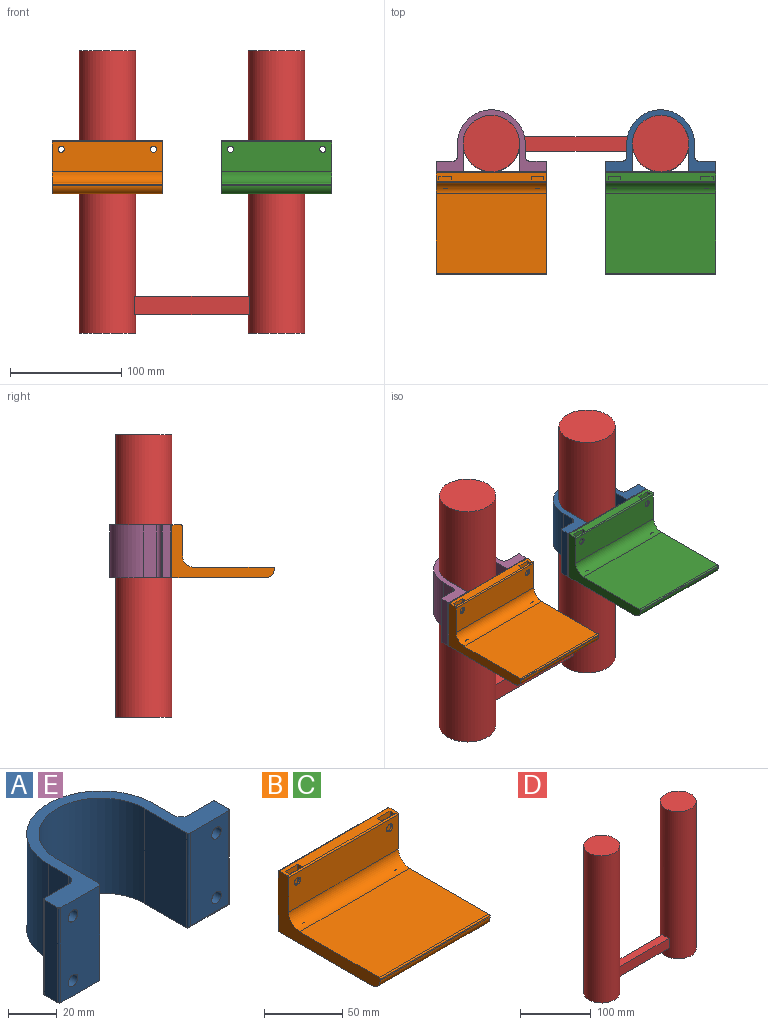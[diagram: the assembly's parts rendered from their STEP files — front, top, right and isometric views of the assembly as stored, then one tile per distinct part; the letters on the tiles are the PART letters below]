
ASSEMBLY  parts=5 mates=10
PART A: 35 faces, bbox 99.1x55.9x47.6 mm
  f0: plane 47.63x24.44mm, normal (1,0,0), area 1163.7mm2, adj f1,f12,f13,f18
  f1: cylinder r=25.4mm len=50.8mm, axis (0,0,-1), area 3800.3mm2, adj f0,f2,f12,f13
  f2: plane 47.63x24.43mm, normal (-1,0,0), area 1163.7mm2, adj f1,f12,f13,f21
  f3: plane 46.66x22.2mm, normal (0,-1,0), area 986.8mm2, adj f12,f19,f20,f21,f23,f26
  f4: plane 47.63x7.59mm, normal (1,0,0), area 361.7mm2, adj f12,f13,f19,f22
  f5: plane 47.63x14.02mm, normal (0,1,0), area 462.5mm2, adj f12,f13,f15,f22,f25,f28
  f6: plane 47.63x11.81mm, normal (1,0,0), area 562.5mm2, adj f7,f12,f13,f15
  f7: cylinder r=30.48mm len=60.96mm, axis (0,0,-1), area 4560.4mm2, adj f6,f8,f12,f13
  f8: plane 47.63x11.81mm, normal (-1,0,0), area 562.5mm2, adj f7,f12,f13,f14
  f9: plane 47.63x14.02mm, normal (0,1,0), area 462.5mm2, adj f12,f13,f14,f16,f31,f34
  f10: plane 47.63x7.59mm, normal (-1,0,0), area 361.7mm2, adj f12,f13,f16,f17
  f11: plane 47.63x22.2mm, normal (0,-1,0), area 1008.2mm2, adj f12,f13,f17,f18,f29,f32
  f12: plane 99.06x55.88mm, normal (0,0,1), area 1072.8mm2, adj f0,f1,f2,f3,f4,f5,f6,f7
  f13: plane 99.06x55.88mm, normal (0,0,-1), area 1049.9mm2, adj f0,f1,f2,f4,f5,f6,f7,f8
  f14: cylinder r=4.06mm len=47.63mm, axis (0,0,1), area 304mm2, adj f8,f9,f12,f13
  f15: cylinder r=4.06mm len=47.63mm, axis (0,0,1), area 304mm2, adj f5,f6,f12,f13
  f16: cylinder r=0.97mm len=47.63mm, axis (0,0,-1), area 72.2mm2, adj f9,f10,f12,f13
  f17: cylinder r=0.97mm len=47.63mm, axis (0,0,-1), area 72.2mm2, adj f10,f11,f12,f13
  f18: cylinder r=0.97mm len=47.63mm, axis (0,0,-1), area 72.2mm2, adj f0,f11,f12,f13
  f19: cylinder r=0.97mm len=47.63mm, axis (0,0,-1), area 71.7mm2, adj f3,f4,f12,f20
  f20: cylinder r=0.97mm len=24.13mm, axis (1,0,0), area 35.5mm2, adj f3,f13,f19,f21
  f21: cylinder r=0.97mm len=47.63mm, axis (0,0,-1), area 71.7mm2, adj f2,f3,f12,f20
  f22: cylinder r=0.97mm len=47.63mm, axis (0,0,-1), area 72.2mm2, adj f4,f5,f12,f13
  f23: cylinder r=2.79mm len=5.59mm, axis (0,1,0), area 89.2mm2, adj f3,f24
  f24: plane 11.43x11.43mm, normal (0,1,0), area 78.1mm2, adj f23,f25
  f25: cylinder r=5.71mm len=11.43mm, axis (0,1,0), area 159.6mm2, adj f5,f24
  f26: cylinder r=2.79mm len=5.59mm, axis (0,1,0), area 89.2mm2, adj f3,f27
  f27: plane 11.43x11.43mm, normal (0,1,0), area 78.1mm2, adj f26,f28
  f28: cylinder r=5.71mm len=11.43mm, axis (0,1,0), area 159.6mm2, adj f5,f27
  f29: cylinder r=2.79mm len=5.59mm, axis (0,1,0), area 89.2mm2, adj f11,f30
  f30: plane 11.43x11.43mm, normal (0,1,0), area 78.1mm2, adj f29,f31
  f31: cylinder r=5.71mm len=11.43mm, axis (0,1,0), area 159.6mm2, adj f9,f30
  f32: cylinder r=2.79mm len=5.59mm, axis (0,1,0), area 89.2mm2, adj f11,f33
  f33: plane 11.43x11.43mm, normal (0,1,0), area 78.1mm2, adj f32,f34
  f34: cylinder r=5.71mm len=11.43mm, axis (0,1,0), area 159.6mm2, adj f9,f33
PART B: 44 faces, bbox 99.1x92.1x47.6 mm
  f0: plane 99.06x7.62mm, normal (0,0,1), area 661.9mm2, adj f8,f9,f12,f15,f35,f36,f37,f38
  f1: cylinder r=2.79mm len=5.59mm, axis (0,1,0), area 22.3mm2, adj f3,f40
  f2: cylinder r=2.79mm len=5.59mm, axis (0,1,0), area 73.6mm2, adj f7,f38
  f3: plane 99.06x26.99mm, normal (0,-1,0), area 2624.3mm2, adj f1,f8,f9,f10,f12,f33
  f4: plane 99.06x71.44mm, normal (0,0,1), area 7076.6mm2, adj f8,f9,f10,f13
  f5: plane 99.06x0.95mm, normal (0,-1,0), area 94.4mm2, adj f8,f9,f11,f13
  f6: plane 99.06x83.5mm, normal (0,0,-1), area 8178.9mm2, adj f8,f9,f11,f14,f16,f17,f18,f19
  f7: plane 99.06x45.72mm, normal (0,1,0), area 4430.9mm2, adj f2,f8,f9,f14,f15,f26,f29,f32
  f8: plane 92.08x47.63mm, normal (1,0,0), area 1248.8mm2, adj f0,f3,f4,f5,f6,f7,f10,f11
  f9: plane 92.08x47.63mm, normal (-1,0,0), area 1248.8mm2, adj f0,f3,f4,f5,f6,f7,f10,f11
  f10: cylinder r=10.16mm len=99.06mm, axis (1,0,0), area 1580.9mm2, adj f3,f4,f8,f9
  f11: cylinder r=7.62mm len=99.06mm, axis (-1,0,0), area 1185.7mm2, adj f5,f6,f8,f9
  f12: cylinder r=0.95mm len=99.06mm, axis (-1,0,0), area 148.2mm2, adj f0,f3,f8,f9
  f13: cylinder r=0.95mm len=99.06mm, axis (-1,0,0), area 148.2mm2, adj f4,f5,f8,f9
  f14: cylinder r=0.95mm len=99.06mm, axis (-1,0,0), area 148.2mm2, adj f6,f7,f8,f9
  f15: cylinder r=0.95mm len=99.06mm, axis (-1,0,0), area 148.2mm2, adj f0,f7,f8,f9
  f16: plane 15.24x4.06mm, normal (1,0,0), area 61.9mm2, adj f6,f17,f19,f20
  f17: plane 15.24x11.43mm, normal (0,1,0), area 149.7mm2, adj f6,f16,f18,f20,f30
  f18: plane 15.24x4.06mm, normal (-1,0,0), area 61.9mm2, adj f6,f17,f19,f20
  f19: plane 15.24x11.43mm, normal (0,-1,0), area 149.7mm2, adj f6,f16,f18,f20,f29
  f20: plane 11.43x4.06mm, normal (0,0,-1), area 46.5mm2, adj f16,f17,f18,f19
  f21: plane 15.24x4.06mm, normal (1,0,0), area 61.9mm2, adj f6,f22,f24,f25
  f22: plane 15.24x11.43mm, normal (0,1,0), area 149.7mm2, adj f6,f21,f23,f25,f28
  f23: plane 15.24x4.06mm, normal (-1,0,0), area 61.9mm2, adj f6,f22,f24,f25
  f24: plane 15.24x11.43mm, normal (0,-1,0), area 149.7mm2, adj f6,f21,f23,f25,f26
  f25: plane 11.43x4.06mm, normal (0,0,-1), area 46.5mm2, adj f21,f22,f23,f24
  f26: cylinder r=2.79mm len=5.59mm, axis (0,1,0), area 73.6mm2, adj f7,f24
  f27: cone r=0mm half-angle=59deg, axis (0,1,0), area 28.6mm2, adj f28
  f28: cylinder r=2.79mm len=6.99mm, axis (0,1,0), area 122.6mm2, adj f22,f27
  f29: cylinder r=2.79mm len=5.59mm, axis (0,1,0), area 73.6mm2, adj f7,f19
  f30: cylinder r=2.79mm len=6.99mm, axis (0,1,0), area 122.6mm2, adj f17,f31
  f31: cone r=0mm half-angle=59deg, axis (0,1,0), area 28.6mm2, adj f30
  f32: cylinder r=2.79mm len=5.59mm, axis (0,1,0), area 73.6mm2, adj f7,f43
  f33: cylinder r=2.79mm len=5.59mm, axis (0,1,0), area 22.3mm2, adj f3,f35
  f34: plane 11.43x4.06mm, normal (0,0,1), area 46.5mm2, adj f35,f36,f37,f38
  f35: plane 15.24x11.43mm, normal (0,1,0), area 149.7mm2, adj f0,f33,f34,f36,f37
  f36: plane 15.24x4.06mm, normal (-1,0,0), area 61.9mm2, adj f0,f34,f35,f38
  f37: plane 15.24x4.06mm, normal (1,0,0), area 61.9mm2, adj f0,f34,f35,f38
  f38: plane 15.24x11.43mm, normal (0,-1,0), area 149.7mm2, adj f0,f2,f34,f36,f37
  f39: plane 11.43x4.06mm, normal (0,0,1), area 46.5mm2, adj f40,f41,f42,f43
  f40: plane 15.24x11.43mm, normal (0,1,0), area 149.7mm2, adj f0,f1,f39,f41,f42
  f41: plane 15.24x4.06mm, normal (1,0,0), area 61.9mm2, adj f0,f39,f40,f43
  f42: plane 15.24x4.06mm, normal (-1,0,0), area 61.9mm2, adj f0,f39,f40,f43
  f43: plane 15.24x11.43mm, normal (0,-1,0), area 149.7mm2, adj f0,f32,f39,f41,f42
PART C: same geometry as B
PART D: 10 faces, bbox 203.2x50.8x254 mm
  f0: cylinder r=25.4mm len=254mm, axis (0,0,-1), area 40313.3mm2, adj f1,f2,f3,f4,f5,f6
  f1: plane 50.8x50.8mm, normal (0,0,1), area 2026.8mm2, adj f0
  f2: plane 50.8x50.8mm, normal (0,0,-1), area 2026.8mm2, adj f0
  f3: plane 103.31x16.88mm, normal (0,-1,0), area 1743.6mm2, adj f0,f5,f6,f7
  f4: plane 103.31x16.88mm, normal (0,1,0), area 1743.6mm2, adj f0,f5,f6,f7
  f5: plane 103.31x13.08mm, normal (0,0,1), area 1336.3mm2, adj f0,f3,f4,f7
  f6: plane 103.31x13.08mm, normal (0,0,-1), area 1336.3mm2, adj f0,f3,f4,f7
  f7: cylinder r=25.4mm len=254mm, axis (0,0,-1), area 40313.3mm2, adj f3,f4,f5,f6,f8,f9
  f8: plane 50.8x50.8mm, normal (0,0,1), area 2026.8mm2, adj f7
  f9: plane 50.8x50.8mm, normal (0,0,-1), area 2026.8mm2, adj f7
PART E: same geometry as A
PLACE A t=(0,0,125.39)mm
PLACE B t=(-152.4,0,125.39)mm
PLACE C t=(0,0,125.39)mm
PLACE D t=(-76.2,0,0)mm
PLACE E t=(-152.4,0,125.39)mm
MATE cylindrical B.f2 <-> E.f29  axis (0,-1,0) through (-193.95,-34.92,165.39)mm
MATE cylindrical C.f1 <-> A.f23  axis (0,-1,0) through (41.55,-34.93,165.39)mm
MATE planar E.f12 <-> A.f12  axis (0,0,1) through (-117.86,-15.88,173.01)mm
MATE planar C.f0 <-> A.f12  axis (0,0,1) through (0,-29.96,173.01)mm
MATE slider E.f1 <-> D.f0  axis (0,0,1) through (-152.4,0,173.01)mm
MATE parallel E.f5 <-> A.f9  axis (0,1,0) through (-110.85,-15.88,149.2)mm
MATE slider A.f1 <-> D.f7  axis (0,0,1) through (0,0,173.01)mm
MATE planar B.f7 <-> E.f11  axis (0,1,0) through (-152.4,-25.4,149.2)mm
MATE planar A.f11 <-> C.f7  axis (0,-1,0) through (-37.27,-25.4,149.2)mm
MATE planar B.f0 <-> E.f12  axis (0,0,1) through (-152.4,-29.96,173.01)mm
